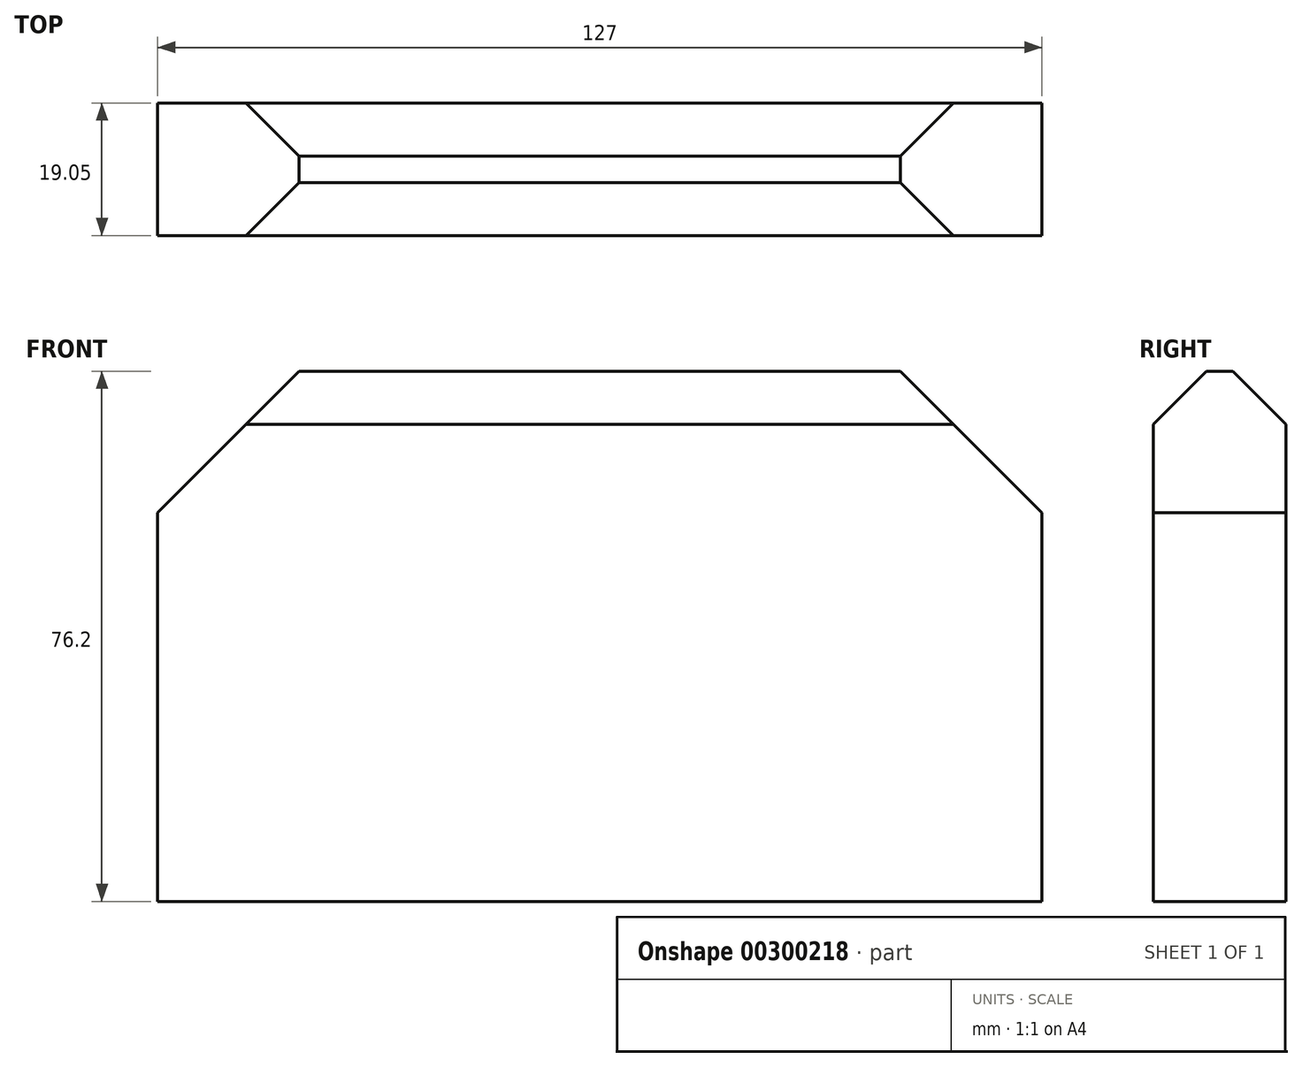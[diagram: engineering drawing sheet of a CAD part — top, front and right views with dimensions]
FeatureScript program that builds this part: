
annotation { "Feature Type Name" : "Feature", "Feature Type Description" : "" }
export const myFeature = defineFeature(function(context is Context, id is Id, definition is map)
    precondition{}
    {
        {
            var Q0;
            Q0=qCreatedBy(makeId("Front.planeOp"),FACE);
            var sketch = newSketch(context, id + "F0", { "sketchPlane" : qUnion([Q0])});
            skLineSegment(sketch, "E0.bottom", {"start": v(-82.29, -14.29) * mm, "end": v(44.71, -14.29) * mm});
            skLineSegment(sketch, "E0.top", {"start": v(-82.29, -90.49) * mm, "end": v(44.71, -90.49) * mm});
            skLineSegment(sketch, "E0.left", {"start": v(-82.29, -14.29) * mm, "end": v(-82.29, -90.49) * mm});
            skLineSegment(sketch, "E0.right", {"start": v(44.71, -14.29) * mm, "end": v(44.71, -90.49) * mm});
            skSolve(sketch);
        }
        {
            var Q0;
            Q0=makeQuery(id+"F0.imprint","IMPRINT",FACE,{"disambiguationData":[TD([[makeQuery(id+"F0.imprint","IMPRINT",EDGE,{"derivedFrom":sQuery(id+"F0.wireOp",EDGE,"E0.bottom")}),-1.0]])]});
            extrude(context, id + "F1", {"entities" : qUnion([Q0]), "depth" : 19.05 * mm});
        }
        {
            var Q0;
            Q0=makeQuery(id+"F1.opExtrude","SWEPT_EDGE",EDGE,{"disambiguationData":[OSD([sQuery(id+"F0.wireOp",EDGE,"E0.bottom"),sQuery(id+"F0.wireOp",EDGE,"E0.right")])]});
            var Q1;
            Q1=makeQuery(id+"F1.opExtrude","SWEPT_EDGE",EDGE,{"disambiguationData":[OSD([sQuery(id+"F0.wireOp",EDGE,"E0.bottom"),sQuery(id+"F0.wireOp",EDGE,"E0.left")])]});
            chamfer(context, id + "F2", {"entities" : qUnion([Q0, Q1]), "width" : 20.32 * mm, "tangentPropagation" : true});
        }
        {
            var Q0;
            Q0=makeQuery(id+"F1.opExtrude","CAP_EDGE",EDGE,{"disambiguationData":[OSD([sQuery(id+"F0.wireOp",EDGE,"E0.bottom")])],"isStart":false});
            var Q1;
            Q1=makeQuery(id+"F1.opExtrude","CAP_EDGE",EDGE,{"disambiguationData":[OSD([sQuery(id+"F0.wireOp",EDGE,"E0.bottom")])],"isStart":true});
            chamfer(context, id + "F3", {"entities" : qUnion([Q0, Q1]), "width" : 7.62 * mm, "tangentPropagation" : true});
        }
    });
